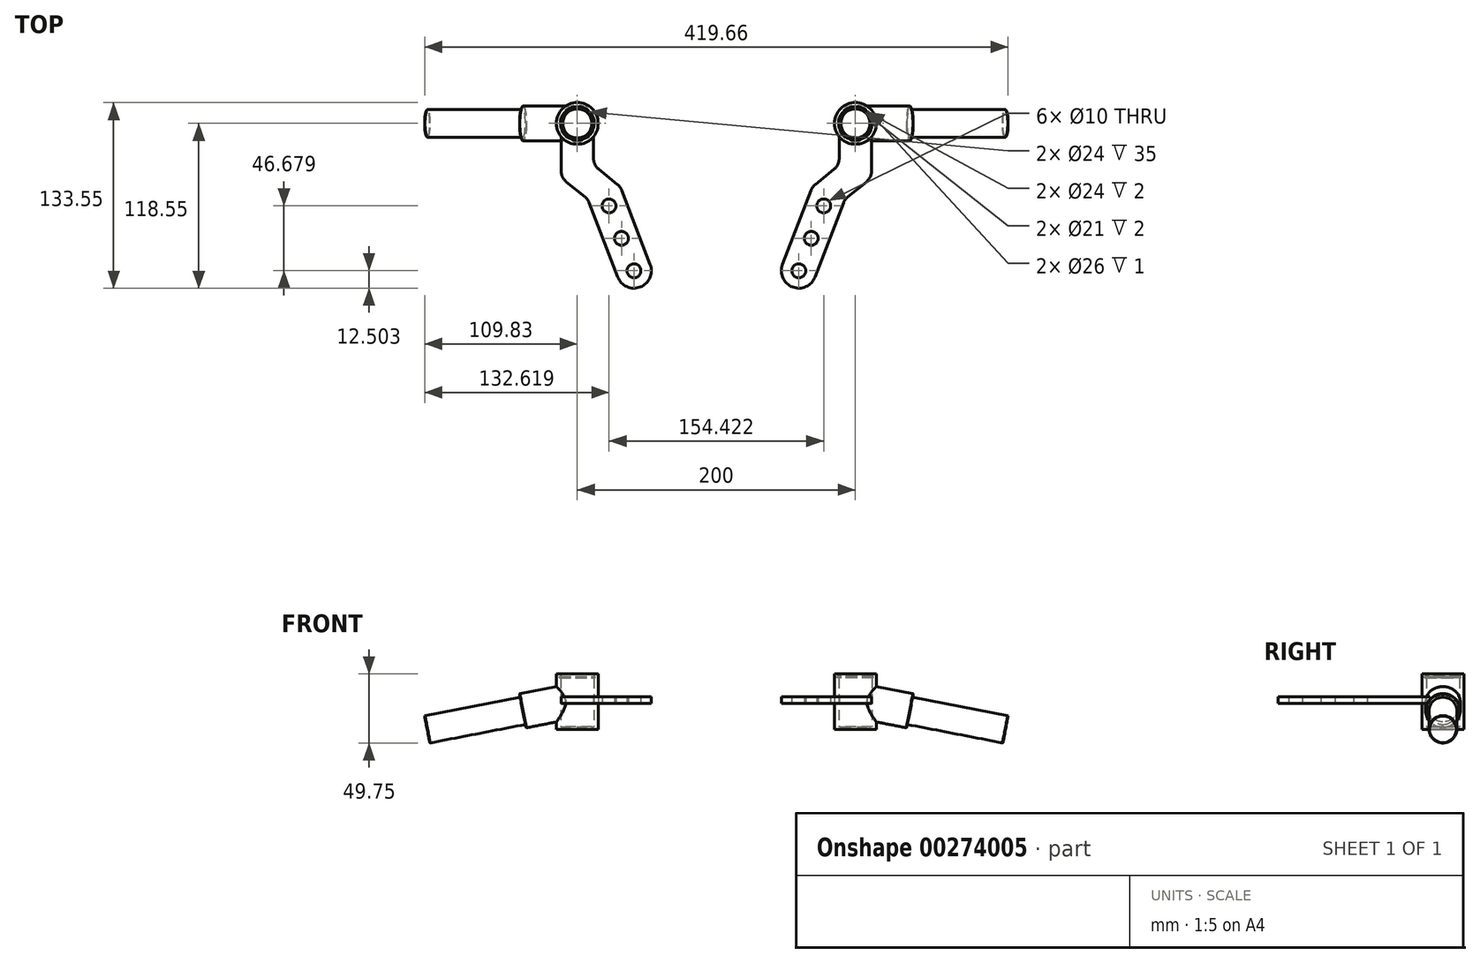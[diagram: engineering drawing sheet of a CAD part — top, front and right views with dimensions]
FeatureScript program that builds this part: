
annotation { "Feature Type Name" : "Feature", "Feature Type Description" : "" }
export const myFeature = defineFeature(function(context is Context, id is Id, definition is map)
    precondition{}
    {
        {
            var Q0;
            Q0=qCreatedBy(makeId("Top.planeOp"),FACE);
            var sketch = newSketch(context, id + "F0", { "sketchPlane" : qUnion([Q0])});
            skCircle(sketch, "E0", {"center": v(0, 0) * mm, "radius": 15 * mm});
            skCircle(sketch, "E1", {"center": v(0, 0) * mm, "radius": 12 * mm});
            skSolve(sketch);
        }
        {
            var Q0;
            Q0=qSketchRegion(id+"F0",true);
            extrude(context, id + "F1", {"entities" : qUnion([Q0]), "endBound" : BoundingType.SYMMETRIC, "depth" : 38 * mm});
        }
        {
            var Q0;
            Q0=makeQuery(id+"F1.opExtrude","CAP_FACE",FACE,{"disambiguationData":[OSD([sQuery(id+"F0.wireOp",EDGE,"E0"),sQuery(id+"F0.wireOp",EDGE,"E1")])],"isStart":true});
            var sketch = newSketch(context, id + "F2", { "sketchPlane" : qUnion([Q0])});
            skCircle(sketch, "E2.0", {"center": v(0, 0) * mm, "radius": 15 * mm});
            skCircle(sketch, "E3", {"center": v(0, 0) * mm, "radius": 10.5 * mm});
            skSolve(sketch);
        }
        {
            var Q0;
            Q0=qSketchRegion(id+"F2",true);
            extrude(context, id + "F3", {"entities" : qUnion([Q0]), "operationType" : NewBodyOperationType.ADD, "depth" : 2 * mm});
        }
        {
            var Q0;
            Q0=qCreatedBy(makeId("Front.planeOp"),FACE);
            var sketch = newSketch(context, id + "F4", { "sketchPlane" : qUnion([Q0])});
            skLineSegment(sketch, "E4.bottom", {"start": v(11, 17) * mm, "end": v(13, 17) * mm});
            skLineSegment(sketch, "E4.top", {"start": v(11, 16) * mm, "end": v(13, 16) * mm});
            skLineSegment(sketch, "E4.left", {"start": v(11, 17) * mm, "end": v(11, 16) * mm});
            skLineSegment(sketch, "E4.right", {"start": v(13, 17) * mm, "end": v(13, 16) * mm});
            skLineSegment(sketch, "E5", {"start": v(0, 0) * mm, "end": v(0, 17.33) * mm, "construction": true});
            skSolve(sketch);
        }
        {
            var Q0;
            Q0=qSketchRegion(id+"F4",true);
            var Q1;
            Q1=sQuery(id+"F4.wireOp",EDGE,"E5");
            revolve(context, id + "F5", {"operationType" : NewBodyOperationType.REMOVE, "entities" : qUnion([Q0]), "axis" : qUnion([Q1]), "revolveType" : RevolveType.FULL, "oppositeDirection" : true});
        }
        {
            var Q0;
            Q0=qCreatedBy(makeId("Right.planeOp"),FACE);
            cPlane(context, id + "F6", {"entities" : qUnion([Q0]), "cplaneType" : CPlaneType.OFFSET, "offset" : 40 * mm, "width" : 150 * mm, "height" : 150 * mm});
        }
        {
            var Q0;
            Q0=qCreatedBy(id+"F6.planeOp",FACE);
            var sketch = newSketch(context, id + "F7", { "sketchPlane" : qUnion([Q0])});
            skCircle(sketch, "E6", {"center": v(0, 0) * mm, "radius": 10 * mm});
            skSolve(sketch);
        }
        {
            var Q0;
            Q0=qSketchRegion(id+"F7",true);
            extrude(context, id + "F8", {"entities" : qUnion([Q0]), "depth" : 70 * mm});
        }
        {
            var Q0;
            Q0=qCreatedBy(makeId("Top.planeOp"),FACE);
            var sketch = newSketch(context, id + "F9", { "sketchPlane" : qUnion([Q0])});
            skLineSegment(sketch, "E7", {"start": v(0, 0) * mm, "end": v(0, -97.15) * mm});
            skSolve(sketch);
        }
        {
            var Q0;
            Q0=makeQuery(id+"F8.opExtrude","SWEPT_BODY",BODY,{"disambiguationData":[OSD([sQuery(id+"F7.wireOp",EDGE,"E6")])]});
            var Q1;
            Q1=sQuery(id+"F9.wireOp",EDGE,"E7");
            transform(context, id + "F10", {"entities" : qUnion([Q0]), "transformType" : TransformType.ROTATION, "transformAxis" : qUnion([Q1]), "angle" : 11 * degree, "oppositeDirection" : true, "makeCopy" : false});
        }
        {
            var Q0;
            Q0=makeQuery(id+"F8.opExtrude","CAP_FACE",FACE,{"disambiguationData":[OSD([sQuery(id+"F7.wireOp",EDGE,"E6")])],"isStart":true});
            var sketch = newSketch(context, id + "F11", { "sketchPlane" : qUnion([Q0])});
            skCircle(sketch, "E8", {"center": v(0, 0) * mm, "radius": 12.5 * mm});
            skSolve(sketch);
        }
        {
            var Q0;
            Q0=qSketchRegion(id+"F11",true);
            var Q1;
            Q1=makeQuery(id+"F3.boolean.opBoolean","MERGE",FACE,{"derivedFrom":[makeQuery(id+"F1.opExtrude","SWEPT_FACE",FACE,{"disambiguationData":[OSD([sQuery(id+"F0.wireOp",EDGE,"E0")])]}),makeQuery(id+"F3.opExtrude","SWEPT_FACE",FACE,{"disambiguationData":[OSD([sQuery(id+"F2.wireOp",EDGE,"E2.0")])]})]});
            extrude(context, id + "F12", {"entities" : qUnion([Q0]), "operationType" : NewBodyOperationType.ADD, "endBound" : BoundingType.UP_TO_SURFACE, "endBoundEntityFace" : qUnion([Q1]), "depth" : 25 * mm});
        }
        {
            var Q0;
            Q0=makeQuery(id+"F8.opExtrude","CAP_EDGE",EDGE,{"disambiguationData":[OSD([sQuery(id+"F7.wireOp",EDGE,"E6")])],"isStart":true});
            var Q1;
            Q1=makeQuery(id+"F8.opExtrude","CAP_EDGE",EDGE,{"disambiguationData":[OSD([sQuery(id+"F7.wireOp",EDGE,"E6")])],"isStart":false});
            var Q2;
            Q2=makeQuery(id+"F12.opExtrude","CAP_EDGE",EDGE,{"disambiguationData":[OSD([sQuery(id+"F11.wireOp",EDGE,"E8")])],"isStart":true});
            chamfer(context, id + "F13", {"entities" : qUnion([Q0, Q1, Q2]), "width" : 0.3 * mm, "tangentPropagation" : true});
        }
        {
            var Q0;
            Q0=qCreatedBy(makeId("Top.planeOp"),FACE);
            var sketch = newSketch(context, id + "F14", { "sketchPlane" : qUnion([Q0])});
            skLineSegment(sketch, "E9", {"start": v(0, 0) * mm, "end": v(0, -72.65) * mm, "construction": true});
            skLineSegment(sketch, "E10", {"start": v(0, 0) * mm, "end": v(-40.7, -106.05) * mm, "construction": true});
            skCircle(sketch, "E11", {"center": v(-40.7, -106.05) * mm, "radius": 5 * mm});
            skCircle(sketch, "E12", {"center": v(-31.75, -82.7) * mm, "radius": 5 * mm});
            skCircle(sketch, "E13", {"center": v(-22.79, -59.37) * mm, "radius": 5 * mm});
            skArc(sketch, "E14", {"start": v(-52.38, -101.57) * mm, "mid": v(-45.19, -117.72) * mm, "end": v(-29.04, -110.53) * mm});
            skLineSegment(sketch, "E15", {"start": v(-52.38, -101.57) * mm, "end": v(-30.88, -45.55) * mm});
            skCircle(sketch, "E16.0", {"center": v(0, 0) * mm, "radius": 15 * mm});
            skLineSegment(sketch, "E17", {"start": v(-11.67, -9.42) * mm, "end": v(-11.67, -30) * mm});
            skLineSegment(sketch, "E18", {"start": v(-11.67, -30) * mm, "end": v(-30.88, -45.55) * mm});
            skLineSegment(sketch, "E19", {"start": v(11.67, -9.42) * mm, "end": v(11.67, -38.96) * mm});
            skLineSegment(sketch, "E20", {"start": v(-29.04, -110.53) * mm, "end": v(-7.54, -54.51) * mm});
            skLineSegment(sketch, "E21", {"start": v(-7.54, -54.51) * mm, "end": v(11.67, -38.96) * mm});
            skSolve(sketch);
        }
        {
            var Q0;
            Q0=makeQuery(id+"F14.imprint","IMPRINT",FACE,{"disambiguationData":[TD([[makeQuery(id+"F14.imprint","IMPRINT",EDGE,{"derivedFrom":sQuery(id+"F14.wireOp",EDGE,"E11")}),-1.0]])]});
            extrude(context, id + "F15", {"entities" : qUnion([Q0]), "endBound" : BoundingType.SYMMETRIC, "depth" : 4.8 * mm});
        }
        {
            var Q0;
            Q0=makeQuery(id+"F15.opExtrude","SWEPT_EDGE",EDGE,{"disambiguationData":[OSD([sQuery(id+"F14.wireOp",EDGE,"E20"),sQuery(id+"F14.wireOp",EDGE,"E21")])]});
            var Q1;
            Q1=makeQuery(id+"F15.opExtrude","SWEPT_EDGE",EDGE,{"disambiguationData":[OSD([sQuery(id+"F14.wireOp",EDGE,"E19"),sQuery(id+"F14.wireOp",EDGE,"E21")])]});
            var Q2;
            Q2=makeQuery(id+"F15.opExtrude","SWEPT_EDGE",EDGE,{"disambiguationData":[OSD([sQuery(id+"F14.wireOp",EDGE,"E15"),sQuery(id+"F14.wireOp",EDGE,"E18")])]});
            var Q3;
            Q3=makeQuery(id+"F15.opExtrude","SWEPT_EDGE",EDGE,{"disambiguationData":[OSD([sQuery(id+"F14.wireOp",EDGE,"E17"),sQuery(id+"F14.wireOp",EDGE,"E18")])]});
            fillet(context, id + "F16", {"entities" : qUnion([Q0, Q1, Q2, Q3]), "radius" : 10 * mm, "tangentPropagation" : true, "allowEdgeOverflow" : false});
        }
        {
            var Q0;
            Q0=qCreatedBy(makeId("Right.planeOp"),FACE);
            cPlane(context, id + "F17", {"entities" : qUnion([Q0]), "cplaneType" : CPlaneType.OFFSET, "offset" : 100 * mm, "oppositeDirection" : true, "width" : 150 * mm, "height" : 150 * mm});
        }
        {
            var Q0;
            Q0=makeQuery(id+"F8.opExtrude","SWEPT_BODY",BODY,{"disambiguationData":[OSD([sQuery(id+"F7.wireOp",EDGE,"E6")])]});
            var Q1;
            Q1=makeQuery(id+"F1.opExtrude","SWEPT_BODY",BODY,{"disambiguationData":[OSD([sQuery(id+"F0.wireOp",EDGE,"E0"),sQuery(id+"F0.wireOp",EDGE,"E1")])]});
            var Q2;
            Q2=makeQuery(id+"F15.opExtrude","SWEPT_BODY",BODY,{"disambiguationData":[OSD([sQuery(id+"F14.wireOp",EDGE,"E11"),sQuery(id+"F14.wireOp",EDGE,"E12"),sQuery(id+"F14.wireOp",EDGE,"E13"),sQuery(id+"F14.wireOp",EDGE,"E14"),sQuery(id+"F14.wireOp",EDGE,"E15"),sQuery(id+"F14.wireOp",EDGE,"E16.0"),sQuery(id+"F14.wireOp",EDGE,"E17"),sQuery(id+"F14.wireOp",EDGE,"E18"),sQuery(id+"F14.wireOp",EDGE,"E19"),sQuery(id+"F14.wireOp",EDGE,"E20"),sQuery(id+"F14.wireOp",EDGE,"E21")])]});
            var Q3;
            Q3=qCreatedBy(id+"F17.planeOp",FACE);
            mirror(context, id + "F18", {"entities" : qUnion([Q0, Q1, Q2]), "mirrorPlane" : qUnion([Q3])});
        }
    });
